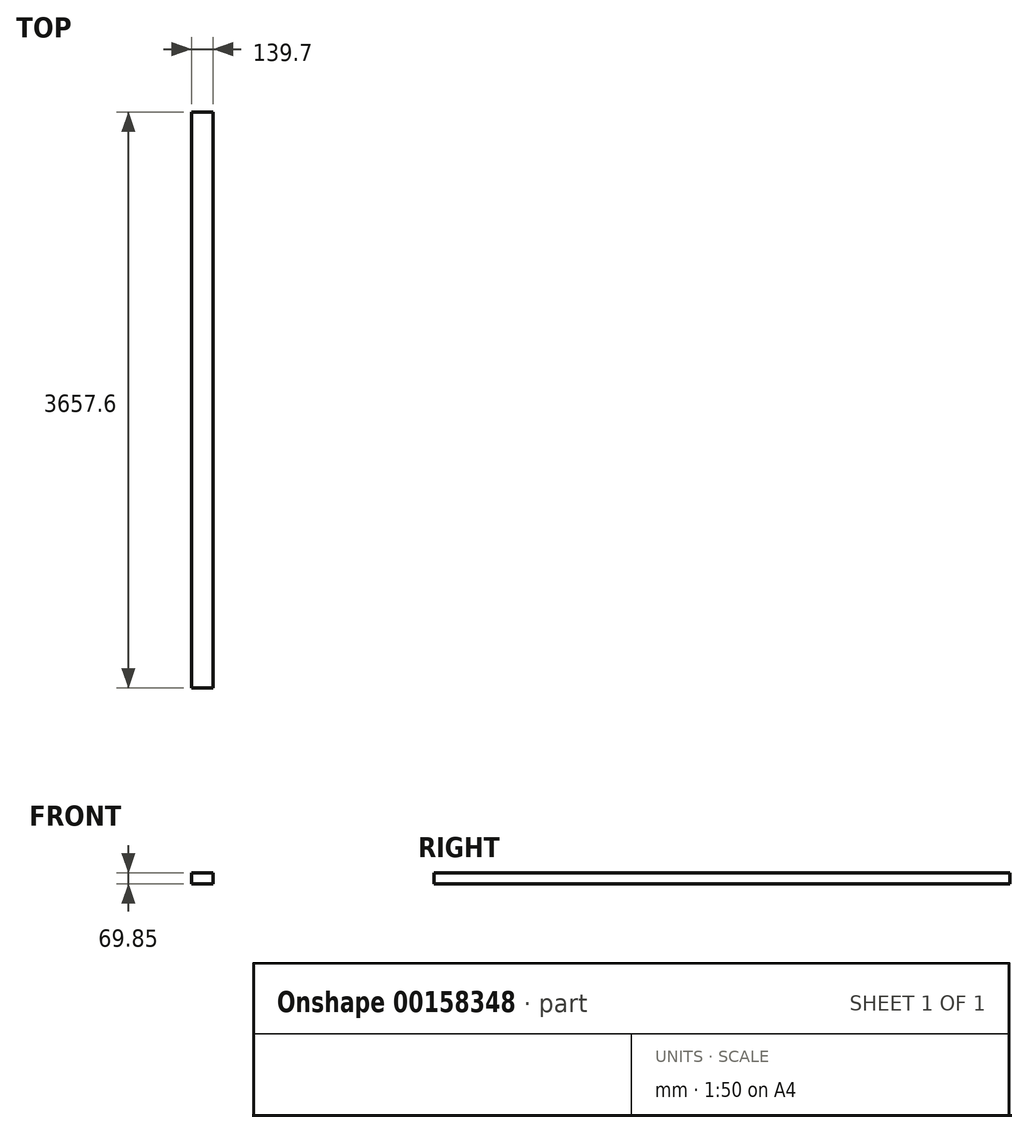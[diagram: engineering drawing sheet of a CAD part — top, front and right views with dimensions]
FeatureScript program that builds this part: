
annotation { "Feature Type Name" : "Feature", "Feature Type Description" : "" }
export const myFeature = defineFeature(function(context is Context, id is Id, definition is map)
    precondition{}
    {
        {
            var Q0;
            Q0=qCreatedBy(makeId("Front.planeOp"),FACE);
            var sketch = newSketch(context, id + "F0", { "sketchPlane" : qUnion([Q0])});
            skLineSegment(sketch, "E0.bottom", {"start": v(-82.1, 44.83) * mm, "end": v(57.6, 44.83) * mm});
            skLineSegment(sketch, "E0.top", {"start": v(-82.1, -25.02) * mm, "end": v(57.6, -25.02) * mm});
            skLineSegment(sketch, "E0.left", {"start": v(-82.1, 44.83) * mm, "end": v(-82.1, -25.02) * mm});
            skLineSegment(sketch, "E0.right", {"start": v(57.6, 44.83) * mm, "end": v(57.6, -25.02) * mm});
            skSolve(sketch);
        }
        {
            var Q0;
            Q0=makeQuery(id+"F0.imprint","IMPRINT",FACE,{"disambiguationData":[TD([[makeQuery(id+"F0.imprint","IMPRINT",EDGE,{"derivedFrom":sQuery(id+"F0.wireOp",EDGE,"E0.bottom")}),-1.0]])]});
            extrude(context, id + "F1", {"entities" : qUnion([Q0]), "endBound" : BoundingType.SYMMETRIC, "depth" : 3657.6 * mm});
        }
    });
